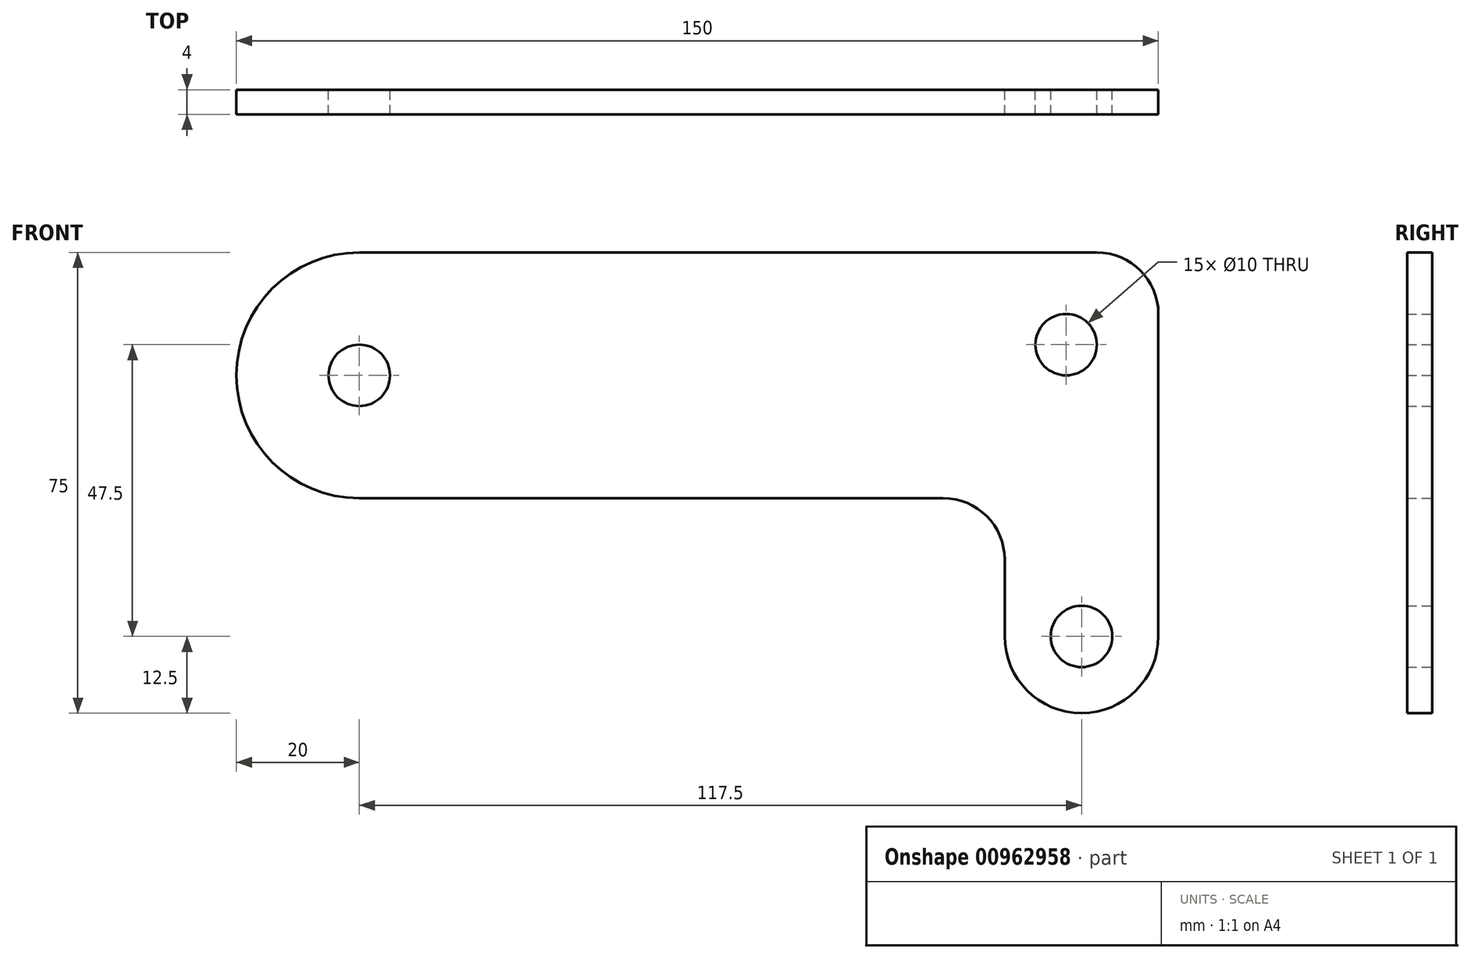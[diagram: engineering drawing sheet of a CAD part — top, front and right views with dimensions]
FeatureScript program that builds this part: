
annotation { "Feature Type Name" : "Feature", "Feature Type Description" : "" }
export const myFeature = defineFeature(function(context is Context, id is Id, definition is map)
    precondition{}
    {
        {
            var Q0;
            Q0=qCreatedBy(makeId("Front.planeOp"),FACE);
            var sketch = newSketch(context, id + "F0", { "sketchPlane" : qUnion([Q0])});
            skLineSegment(sketch, "E0", {"start": v(0, 0) * mm, "end": v(120, 0) * mm});
            skArc(sketch, "E1", {"start": v(120, 0) * mm, "mid": v(127.07, -2.93) * mm, "end": v(130, -10) * mm});
            skLineSegment(sketch, "E2", {"start": v(130, -10) * mm, "end": v(130, -62.5) * mm});
            skArc(sketch, "E3", {"start": v(130, -62.5) * mm, "mid": v(117.5, -75) * mm, "end": v(105, -62.5) * mm});
            skLineSegment(sketch, "E4", {"start": v(105, -62.5) * mm, "end": v(105, -50) * mm});
            skArc(sketch, "E5", {"start": v(105, -50) * mm, "mid": v(102.07, -42.93) * mm, "end": v(95, -40) * mm});
            skLineSegment(sketch, "E6", {"start": v(95, -40) * mm, "end": v(0, -40) * mm});
            skArc(sketch, "E7", {"start": v(0, -40) * mm, "mid": v(-20, -20) * mm, "end": v(0, 0) * mm});
            skCircle(sketch, "E8", {"center": v(115, -15) * mm, "radius": 5 * mm});
            skCircle(sketch, "E9", {"center": v(0, -20) * mm, "radius": 5 * mm});
            skCircle(sketch, "E10", {"center": v(117.5, -62.5) * mm, "radius": 5 * mm});
            skSolve(sketch);
        }
        {
            var Q0;
            Q0 = qSketchRegion(id + "F0", true);
            extrude(context, id + "F1", {"entities" : qUnion([Q0]), "depth" : 4 * mm, "offsetDistance" : 25 * mm, "symmetric" : true});
        }
    });
